# Revit family: QF_BOURGEAT_Satellite4G_GN6_pietement_froid
name_source: partatom
category: Equipement spécialisé
revit_build: Autodesk Revit 2015 (Build: 20140606_1530(x64)
units: mm (PartAtom-declared; Revit-internal decimal feet)

## types (2) — shared parameters
Certification = NF hygiene alimentaire
Charge max = 60.00 kg
Charge_gaz = 0.150 Kg
Classe Climatique = 4
Consommation énergétique = 2.4Kwh/h NFD40-016
Diametre_roue = 80 mm  [stored 0.262467 ft]
Fabricant = BOURGEAT
Fréquence = 50 Hz
Hauteur hors tout = 1519 mm  [stored 4.9836 ft]
Hauteur_poignee_porte_sol = 280 mm  [stored 0.918635 ft]
Hauteur_poignees_laterales = 804 mm  [stored 2.6378 ft]
Hauteur_porte = 687 mm
Hauteur_roue = 792 mm  [stored 2.59843 ft]
Indice de protection = IP25
Intensite = 1 A
Largeur_porte = 706 mm  [stored 2.31627 ft]
Longueur hors tout = 752 mm  [stored 2.46719 ft]
Longueur_poignees_laterales = 609 mm  [stored 1.99803 ft]
Materiau_Poignee_porte = B_Elastomère_TPE_S
Materiau_bac = B_Elastomère_TPE_S
Materiau_bandage = B_Elastomère_TPE_S
Materiau_porte = Acier inoxydable, brossé
Materiau_vitre = Verre, vitrage transparent, trempé
Nature isolant = Mousse sans PU
Phase = 2
Pos_V_IHM = 38 mm  [stored 0.124672 ft]
Profondeur hors tout = 765 mm  [stored 2.50984 ft]
Puissance frigorifique = 270 W à-5°C
Puissance électrique  = 300 W
Spécification du Fabricant = Satellite 4G
Tension = 230 V
Type Fluide Frigorigène = R134a
URL catalogue = http://www.bourgeat.fr

## per-type parameters (varying)
| type | Modèle | Poids net à vide | Poignee_droite | Poignee_gauche |
| GN6_1/1_entrree530_porte_inox_tirant_droit | 842006 + 844000 + 844015 | 650.00 kg | Oui | Non |
| GN6_1/1_entrree530_porte_inox_tirant_gauche | 842006 + 844015 | 65.00 kg | Non | Oui |

note: [stored X ft] marks values corroborated as IEEE doubles in the binary element streams (Revit-internal decimal feet)
